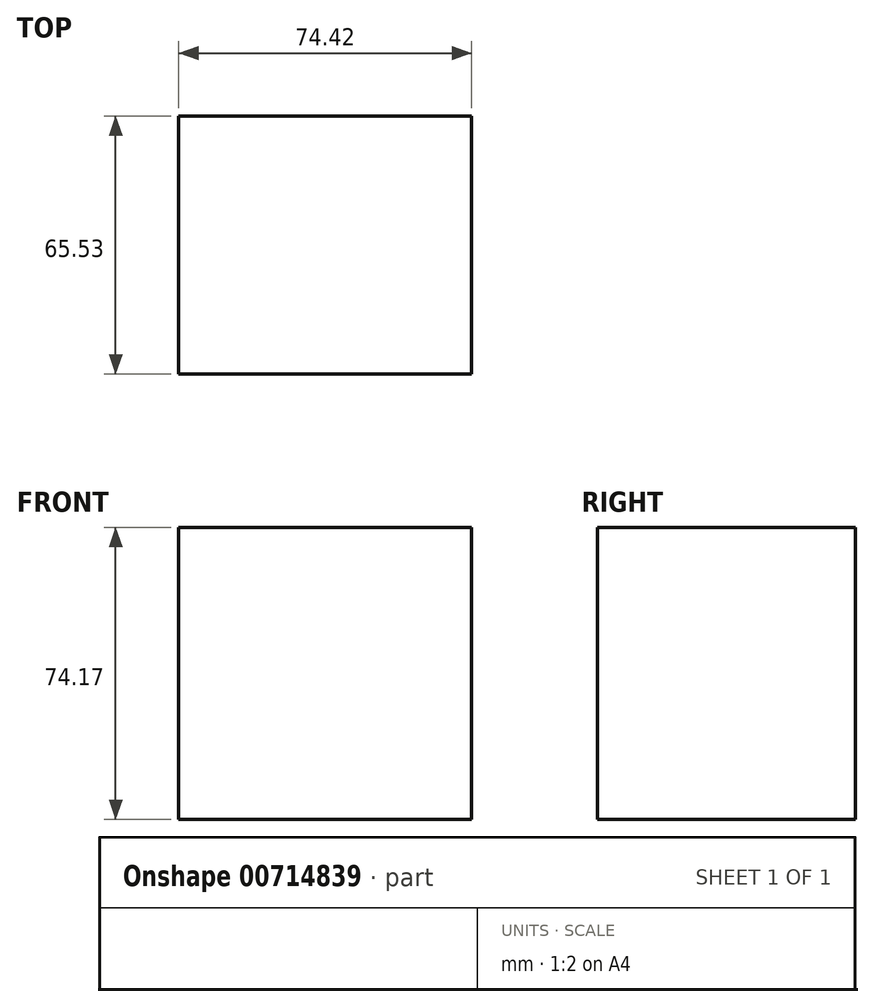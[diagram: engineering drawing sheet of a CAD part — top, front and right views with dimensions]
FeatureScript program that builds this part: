
annotation { "Feature Type Name" : "Feature", "Feature Type Description" : "" }
export const myFeature = defineFeature(function(context is Context, id is Id, definition is map)
    precondition{}
    {
        {
            var Q0;
            Q0=qCreatedBy(makeId("Front.planeOp"),FACE);
            var sketch = newSketch(context, id + "F0", { "sketchPlane" : qUnion([Q0])});
            skLineSegment(sketch, "E0.bottom", {"start": v(-25, 26.15) * mm, "end": v(49.42, 26.15) * mm});
            skLineSegment(sketch, "E0.top", {"start": v(-25, -48.02) * mm, "end": v(49.42, -48.02) * mm});
            skLineSegment(sketch, "E0.left", {"start": v(-25, 26.15) * mm, "end": v(-25, -48.02) * mm});
            skLineSegment(sketch, "E0.right", {"start": v(49.42, 26.15) * mm, "end": v(49.42, -48.02) * mm});
            skSolve(sketch);
        }
        {
            var Q0;
            Q0 = qSketchRegion(id + "F0", true);
            extrude(context, id + "F1", {"entities" : qUnion([Q0]), "depth" : 65.53 * mm, "offsetDistance" : 25.4 * mm});
        }
        {
            var Q0;
            Q0=qCreatedBy(makeId("Front.planeOp"),FACE);
            var sketch = newSketch(context, id + "F2", { "sketchPlane" : qUnion([Q0])});
            skCircle(sketch, "E1", {"center": v(7.4, -9.11) * mm, "radius": 11.74 * mm});
            skPoint(sketch, "E1.first.point", {"position": v(0, 0) * mm});
            skPoint(sketch, "E1.second.point", {"position": v(14.78, 0) * mm});
            skPoint(sketch, "E1.third.point", {"position": v(11.32, -20.17) * mm});
            skSolve(sketch);
        }
        {
            var Q0;
            Q0=sQuery(id+"F2.wireOp",EDGE,"E1");
            extrude(context, id + "F3", {"bodyType" : ToolBodyType.SURFACE, "surfaceEntities" : qUnion([Q0]), "depth" : 3657.6 * mm, "offsetDistance" : 25.4 * mm});
        }
    });
